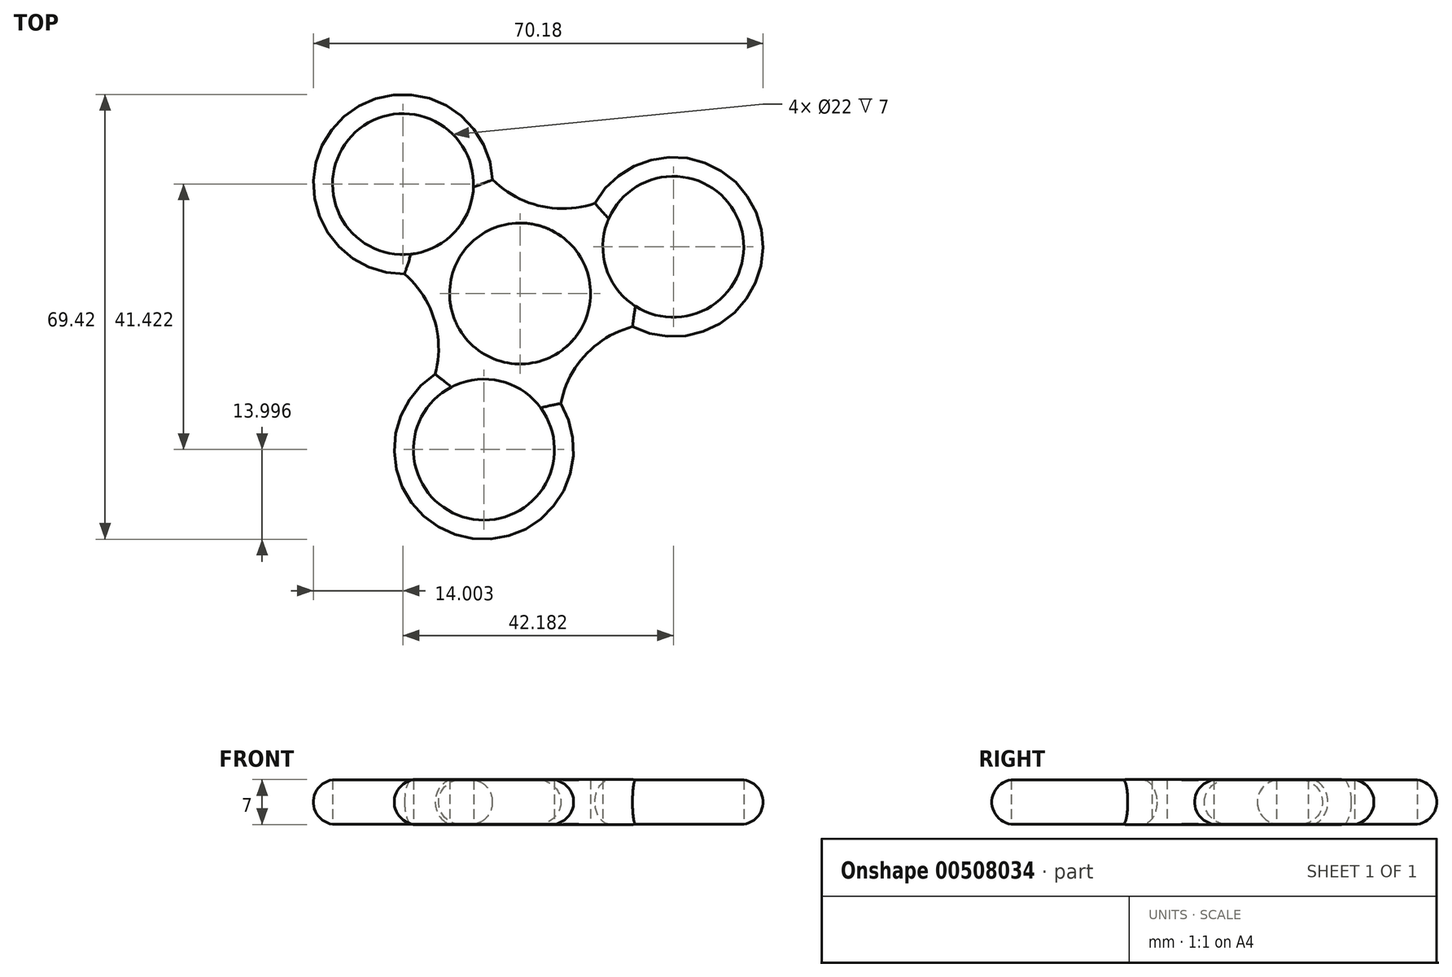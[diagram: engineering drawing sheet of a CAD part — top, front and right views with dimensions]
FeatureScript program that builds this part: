
annotation { "Feature Type Name" : "Feature", "Feature Type Description" : "" }
export const myFeature = defineFeature(function(context is Context, id is Id, definition is map)
    precondition{}
    {
        {
            var Q0;
            Q0=qCreatedBy(makeId("Top.planeOp"),FACE);
            var sketch = newSketch(context, id + "F0", { "sketchPlane" : qUnion([Q0])});
            skCircle(sketch, "E0", {"center": v(0, 0) * mm, "radius": 11 * mm});
            skLineSegment(sketch, "E1", {"start": v(0, 0) * mm, "end": v(-18.27, 17.07) * mm});
            skLineSegment(sketch, "E2", {"start": v(0, 0) * mm, "end": v(23.91, 7.29) * mm});
            skLineSegment(sketch, "E3", {"start": v(0, 0) * mm, "end": v(-5.65, -24.35) * mm});
            skCircle(sketch, "E4", {"center": v(-18.27, 17.07) * mm, "radius": 11 * mm});
            skCircle(sketch, "E5", {"center": v(23.91, 7.29) * mm, "radius": 11 * mm});
            skCircle(sketch, "E6", {"center": v(-5.65, -24.35) * mm, "radius": 11 * mm});
            skCircle(sketch, "E7", {"center": v(0, 0) * mm, "radius": 14 * mm});
            skCircle(sketch, "E8", {"center": v(-18.27, 17.07) * mm, "radius": 14 * mm});
            skCircle(sketch, "E9", {"center": v(23.91, 7.29) * mm, "radius": 14 * mm});
            skCircle(sketch, "E10", {"center": v(-5.65, -24.35) * mm, "radius": 14 * mm});
            skLineSegment(sketch, "E11", {"start": v(-18.27, 17.07) * mm, "end": v(-8.7, 27.3) * mm});
            skLineSegment(sketch, "E12", {"start": v(23.91, 7.29) * mm, "end": v(19.84, 20.68) * mm});
            skLineSegment(sketch, "E13", {"start": v(-5.65, -24.35) * mm, "end": v(7.99, -27.52) * mm});
            skLineSegment(sketch, "E14", {"start": v(-5.65, -24.35) * mm, "end": v(-19.29, -21.2) * mm});
            skLineSegment(sketch, "E15", {"start": v(-18.27, 17.07) * mm, "end": v(-27.82, 6.84) * mm});
            skLineSegment(sketch, "E16", {"start": v(23.91, 7.29) * mm, "end": v(28, -6.1) * mm});
            skArc(sketch, "E17", {"start": v(-8.7, 27.3) * mm, "mid": v(3.16, 13.64) * mm, "end": v(19.84, 20.68) * mm});
            skArc(sketch, "E18", {"start": v(-19.29, -21.2) * mm, "mid": v(-13.4, -4.08) * mm, "end": v(-27.82, 6.84) * mm});
            skArc(sketch, "E19", {"start": v(28, -6.1) * mm, "mid": v(10.23, -9.56) * mm, "end": v(7.99, -27.52) * mm});
            skSolve(sketch);
        }
        {
            var Q0;
            {var subQ0=sQuery(id+"F0.wireOp",EDGE,"E17");var subQ1=sQuery(id+"F0.wireOp",EDGE,"E7");var subQ2=makeQuery(id+"F0.imprint","INTERSECT",VERTEX,{"derivedFrom":[subQ1,subQ0]});Q0=makeQuery(id+"F0.imprint","IMPRINT",FACE,{"disambiguationData":[TD([[makeQuery(id+"F0.imprint","IMPRINT",EDGE,{"disambiguationData":[TD([[subQ2,1.0]])],"derivedFrom":subQ1}),-1.0]])]});}
            var Q1;
            {var subQ0=sQuery(id+"F0.wireOp",EDGE,"E17");var subQ1=sQuery(id+"F0.wireOp",EDGE,"E7");var subQ2=makeQuery(id+"F0.imprint","INTERSECT",VERTEX,{"derivedFrom":[subQ1,subQ0]});Q1=makeQuery(id+"F0.imprint","IMPRINT",FACE,{"disambiguationData":[TD([[makeQuery(id+"F0.imprint","IMPRINT",EDGE,{"disambiguationData":[TD([[subQ2,-1.0]])],"derivedFrom":subQ1}),-1.0]])]});}
            var Q2;
            {var subQ0=sQuery(id+"F0.wireOp",EDGE,"E18");var subQ1=sQuery(id+"F0.wireOp",EDGE,"E7");var subQ2=makeQuery(id+"F0.imprint","INTERSECT",VERTEX,{"derivedFrom":[subQ1,subQ0]});Q2=makeQuery(id+"F0.imprint","IMPRINT",FACE,{"disambiguationData":[TD([[makeQuery(id+"F0.imprint","IMPRINT",EDGE,{"disambiguationData":[TD([[subQ2,1.0]])],"derivedFrom":subQ1}),-1.0]])]});}
            var Q3;
            {var subQ0=sQuery(id+"F0.wireOp",EDGE,"E18");var subQ1=sQuery(id+"F0.wireOp",EDGE,"E7");var subQ2=makeQuery(id+"F0.imprint","INTERSECT",VERTEX,{"derivedFrom":[subQ1,subQ0]});Q3=makeQuery(id+"F0.imprint","IMPRINT",FACE,{"disambiguationData":[TD([[makeQuery(id+"F0.imprint","IMPRINT",EDGE,{"disambiguationData":[TD([[subQ2,-1.0]])],"derivedFrom":subQ1}),-1.0]])]});}
            var Q4;
            {var subQ0=sQuery(id+"F0.wireOp",EDGE,"E19");var subQ1=sQuery(id+"F0.wireOp",EDGE,"E7");var subQ2=makeQuery(id+"F0.imprint","INTERSECT",VERTEX,{"derivedFrom":[subQ1,subQ0]});Q4=makeQuery(id+"F0.imprint","IMPRINT",FACE,{"disambiguationData":[TD([[makeQuery(id+"F0.imprint","IMPRINT",EDGE,{"disambiguationData":[TD([[subQ2,1.0]])],"derivedFrom":subQ1}),-1.0]])]});}
            var Q5;
            {var subQ0=sQuery(id+"F0.wireOp",EDGE,"E19");var subQ1=sQuery(id+"F0.wireOp",EDGE,"E7");var subQ2=makeQuery(id+"F0.imprint","INTERSECT",VERTEX,{"derivedFrom":[subQ1,subQ0]});Q5=makeQuery(id+"F0.imprint","IMPRINT",FACE,{"disambiguationData":[TD([[makeQuery(id+"F0.imprint","IMPRINT",EDGE,{"disambiguationData":[TD([[subQ2,-1.0]])],"derivedFrom":subQ1}),-1.0]])]});}
            var Q6;
            {var subQ0=sQuery(id+"F0.wireOp",EDGE,"E15");var subQ1=sQuery(id+"F0.wireOp",EDGE,"E4");var subQ2=makeQuery(id+"F0.imprint","INTERSECT",VERTEX,{"derivedFrom":[subQ1,subQ0]});Q6=makeQuery(id+"F0.imprint","IMPRINT",FACE,{"disambiguationData":[TD([[makeQuery(id+"F0.imprint","IMPRINT",EDGE,{"disambiguationData":[TD([[subQ2,1.0]])],"derivedFrom":subQ1}),-1.0]])]});}
            var Q7;
            {var subQ0=sQuery(id+"F0.wireOp",EDGE,"E12");var subQ1=sQuery(id+"F0.wireOp",EDGE,"E5");var subQ2=makeQuery(id+"F0.imprint","INTERSECT",VERTEX,{"derivedFrom":[subQ1,subQ0]});Q7=makeQuery(id+"F0.imprint","IMPRINT",FACE,{"disambiguationData":[TD([[makeQuery(id+"F0.imprint","IMPRINT",EDGE,{"disambiguationData":[TD([[subQ2,1.0]])],"derivedFrom":subQ1}),-1.0]])]});}
            var Q8;
            {var subQ0=sQuery(id+"F0.wireOp",EDGE,"E14");var subQ1=sQuery(id+"F0.wireOp",EDGE,"E6");var subQ2=makeQuery(id+"F0.imprint","INTERSECT",VERTEX,{"derivedFrom":[subQ1,subQ0]});Q8=makeQuery(id+"F0.imprint","IMPRINT",FACE,{"disambiguationData":[TD([[makeQuery(id+"F0.imprint","IMPRINT",EDGE,{"disambiguationData":[TD([[subQ2,-1.0]])],"derivedFrom":subQ1}),-1.0]])]});}
            var Q9;
            {var subQ1=sQuery(id+"F0.wireOp",EDGE,"E7");var subQ5=makeQuery(id+"F0.imprint","INTERSECT",VERTEX,{"derivedFrom":[subQ1,sQuery(id+"F0.wireOp",EDGE,"E17")]});Q9=makeQuery(id+"F0.imprint","IMPRINT",FACE,{"disambiguationData":[TD([[makeQuery(id+"F0.imprint","IMPRINT",EDGE,{"disambiguationData":[TD([[subQ5,1.0]])],"derivedFrom":subQ1}),1.0]])]});}
            var Q10;
            {var subQ1=sQuery(id+"F0.wireOp",EDGE,"E7");var subQ5=makeQuery(id+"F0.imprint","INTERSECT",VERTEX,{"derivedFrom":[subQ1,sQuery(id+"F0.wireOp",EDGE,"E18")]});Q10=makeQuery(id+"F0.imprint","IMPRINT",FACE,{"disambiguationData":[TD([[makeQuery(id+"F0.imprint","IMPRINT",EDGE,{"disambiguationData":[TD([[subQ5,1.0]])],"derivedFrom":subQ1}),1.0]])]});}
            var Q11;
            {var subQ1=sQuery(id+"F0.wireOp",EDGE,"E7");var subQ5=makeQuery(id+"F0.imprint","INTERSECT",VERTEX,{"derivedFrom":[subQ1,sQuery(id+"F0.wireOp",EDGE,"E19")]});Q11=makeQuery(id+"F0.imprint","IMPRINT",FACE,{"disambiguationData":[TD([[makeQuery(id+"F0.imprint","IMPRINT",EDGE,{"disambiguationData":[TD([[subQ5,1.0]])],"derivedFrom":subQ1}),1.0]])]});}
            var Q12;
            {var subQ0=sQuery(id+"F0.wireOp",EDGE,"E18");var subQ1=sQuery(id+"F0.wireOp",EDGE,"E8");var subQ2=makeQuery(id+"F0.imprint","INTERSECT",VERTEX,{"derivedFrom":[subQ1,subQ0]});Q12=makeQuery(id+"F0.imprint","IMPRINT",FACE,{"disambiguationData":[TD([[makeQuery(id+"F0.imprint","IMPRINT",EDGE,{"disambiguationData":[TD([[subQ2,-1.0]])],"derivedFrom":subQ1}),1.0]])]});}
            var Q13;
            {var subQ0=sQuery(id+"F0.wireOp",EDGE,"E17");var subQ2=sQuery(id+"F0.wireOp",EDGE,"E8");var subQ6=makeQuery(id+"F0.imprint","INTERSECT",VERTEX,{"derivedFrom":[subQ2,subQ0]});Q13=makeQuery(id+"F0.imprint","IMPRINT",FACE,{"disambiguationData":[TD([[makeQuery(id+"F0.imprint","IMPRINT",EDGE,{"disambiguationData":[TD([[subQ6,1.0]])],"derivedFrom":subQ2}),1.0]])]});}
            var Q14;
            {var subQ0=sQuery(id+"F0.wireOp",EDGE,"E17");var subQ2=sQuery(id+"F0.wireOp",EDGE,"E9");var subQ6=makeQuery(id+"F0.imprint","INTERSECT",VERTEX,{"derivedFrom":[subQ2,subQ0]});Q14=makeQuery(id+"F0.imprint","IMPRINT",FACE,{"disambiguationData":[TD([[makeQuery(id+"F0.imprint","IMPRINT",EDGE,{"disambiguationData":[TD([[subQ6,-1.0]])],"derivedFrom":subQ2}),1.0]])]});}
            var Q15;
            {var subQ0=sQuery(id+"F0.wireOp",EDGE,"E19");var subQ2=sQuery(id+"F0.wireOp",EDGE,"E9");var subQ9=makeQuery(id+"F0.imprint","INTERSECT",VERTEX,{"derivedFrom":[subQ2,subQ0]});Q15=makeQuery(id+"F0.imprint","IMPRINT",FACE,{"disambiguationData":[TD([[makeQuery(id+"F0.imprint","IMPRINT",EDGE,{"disambiguationData":[TD([[subQ9,1.0]])],"derivedFrom":subQ2}),1.0]])]});}
            var Q16;
            {var subQ0=sQuery(id+"F0.wireOp",EDGE,"E19");var subQ1=sQuery(id+"F0.wireOp",EDGE,"E10");var subQ2=makeQuery(id+"F0.imprint","INTERSECT",VERTEX,{"derivedFrom":[subQ1,subQ0]});Q16=makeQuery(id+"F0.imprint","IMPRINT",FACE,{"disambiguationData":[TD([[makeQuery(id+"F0.imprint","IMPRINT",EDGE,{"disambiguationData":[TD([[subQ2,-1.0]])],"derivedFrom":subQ1}),1.0]])]});}
            var Q17;
            {var subQ0=sQuery(id+"F0.wireOp",EDGE,"E8");var subQ3=sQuery(id+"F0.wireOp",EDGE,"E7");var subQ5=makeQuery(id+"F0.imprint","INTERSECT",VERTEX,{"disambiguationData":[OD(1.0)],"derivedFrom":[subQ3,subQ0]});Q17=makeQuery(id+"F0.imprint","IMPRINT",FACE,{"disambiguationData":[TD([[makeQuery(id+"F0.imprint","IMPRINT",EDGE,{"disambiguationData":[TD([[subQ5,1.0]])],"derivedFrom":subQ3}),1.0]])]});}
            var Q18;
            {var subQ0=sQuery(id+"F0.wireOp",EDGE,"E8");var subQ3=sQuery(id+"F0.wireOp",EDGE,"E7");var subQ5=makeQuery(id+"F0.imprint","INTERSECT",VERTEX,{"disambiguationData":[OD(0.0)],"derivedFrom":[subQ3,subQ0]});Q18=makeQuery(id+"F0.imprint","IMPRINT",FACE,{"disambiguationData":[TD([[makeQuery(id+"F0.imprint","IMPRINT",EDGE,{"disambiguationData":[TD([[subQ5,-1.0]])],"derivedFrom":subQ3}),1.0]])]});}
            var Q19;
            {var subQ0=sQuery(id+"F0.wireOp",EDGE,"E9");var subQ3=sQuery(id+"F0.wireOp",EDGE,"E7");var subQ5=makeQuery(id+"F0.imprint","INTERSECT",VERTEX,{"disambiguationData":[OD(0.0)],"derivedFrom":[subQ3,subQ0]});Q19=makeQuery(id+"F0.imprint","IMPRINT",FACE,{"disambiguationData":[TD([[makeQuery(id+"F0.imprint","IMPRINT",EDGE,{"disambiguationData":[TD([[subQ5,1.0]])],"derivedFrom":subQ3}),1.0]])]});}
            var Q20;
            {var subQ0=sQuery(id+"F0.wireOp",EDGE,"E9");var subQ3=sQuery(id+"F0.wireOp",EDGE,"E7");var subQ5=makeQuery(id+"F0.imprint","INTERSECT",VERTEX,{"disambiguationData":[OD(1.0)],"derivedFrom":[subQ3,subQ0]});Q20=makeQuery(id+"F0.imprint","IMPRINT",FACE,{"disambiguationData":[TD([[makeQuery(id+"F0.imprint","IMPRINT",EDGE,{"disambiguationData":[TD([[subQ5,-1.0]])],"derivedFrom":subQ3}),1.0]])]});}
            var Q21;
            {var subQ0=sQuery(id+"F0.wireOp",EDGE,"E10");var subQ3=sQuery(id+"F0.wireOp",EDGE,"E7");var subQ5=makeQuery(id+"F0.imprint","INTERSECT",VERTEX,{"disambiguationData":[OD(1.0)],"derivedFrom":[subQ3,subQ0]});Q21=makeQuery(id+"F0.imprint","IMPRINT",FACE,{"disambiguationData":[TD([[makeQuery(id+"F0.imprint","IMPRINT",EDGE,{"disambiguationData":[TD([[subQ5,1.0]])],"derivedFrom":subQ3}),1.0]])]});}
            var Q22;
            {var subQ0=sQuery(id+"F0.wireOp",EDGE,"E10");var subQ3=sQuery(id+"F0.wireOp",EDGE,"E7");var subQ5=makeQuery(id+"F0.imprint","INTERSECT",VERTEX,{"disambiguationData":[OD(0.0)],"derivedFrom":[subQ3,subQ0]});Q22=makeQuery(id+"F0.imprint","IMPRINT",FACE,{"disambiguationData":[TD([[makeQuery(id+"F0.imprint","IMPRINT",EDGE,{"disambiguationData":[TD([[subQ5,-1.0]])],"derivedFrom":subQ3}),1.0]])]});}
            var Q23;
            {var subQ0=sQuery(id+"F0.wireOp",EDGE,"E17");var subQ1=sQuery(id+"F0.wireOp",EDGE,"E8");var subQ3=makeQuery(id+"F0.imprint","INTERSECT",VERTEX,{"derivedFrom":[subQ1,subQ0]});Q23=makeQuery(id+"F0.imprint","IMPRINT",FACE,{"disambiguationData":[TD([[makeQuery(id+"F0.imprint","IMPRINT",EDGE,{"disambiguationData":[TD([[subQ3,-1.0]])],"derivedFrom":subQ1}),1.0]])]});}
            var Q24;
            {var subQ0=sQuery(id+"F0.wireOp",EDGE,"E17");var subQ1=sQuery(id+"F0.wireOp",EDGE,"E9");var subQ3=makeQuery(id+"F0.imprint","INTERSECT",VERTEX,{"derivedFrom":[subQ1,subQ0]});Q24=makeQuery(id+"F0.imprint","IMPRINT",FACE,{"disambiguationData":[TD([[makeQuery(id+"F0.imprint","IMPRINT",EDGE,{"disambiguationData":[TD([[subQ3,1.0]])],"derivedFrom":subQ1}),1.0]])]});}
            var Q25;
            {var subQ0=sQuery(id+"F0.wireOp",EDGE,"E19");var subQ1=sQuery(id+"F0.wireOp",EDGE,"E9");var subQ3=makeQuery(id+"F0.imprint","INTERSECT",VERTEX,{"derivedFrom":[subQ1,subQ0]});Q25=makeQuery(id+"F0.imprint","IMPRINT",FACE,{"disambiguationData":[TD([[makeQuery(id+"F0.imprint","IMPRINT",EDGE,{"disambiguationData":[TD([[subQ3,-1.0]])],"derivedFrom":subQ1}),1.0]])]});}
            var Q26;
            {var subQ0=sQuery(id+"F0.wireOp",EDGE,"E19");var subQ1=sQuery(id+"F0.wireOp",EDGE,"E10");var subQ3=makeQuery(id+"F0.imprint","INTERSECT",VERTEX,{"derivedFrom":[subQ1,subQ0]});Q26=makeQuery(id+"F0.imprint","IMPRINT",FACE,{"disambiguationData":[TD([[makeQuery(id+"F0.imprint","IMPRINT",EDGE,{"disambiguationData":[TD([[subQ3,1.0]])],"derivedFrom":subQ1}),1.0]])]});}
            var Q27;
            {var subQ0=sQuery(id+"F0.wireOp",EDGE,"E18");var subQ1=sQuery(id+"F0.wireOp",EDGE,"E8");var subQ3=makeQuery(id+"F0.imprint","INTERSECT",VERTEX,{"derivedFrom":[subQ1,subQ0]});Q27=makeQuery(id+"F0.imprint","IMPRINT",FACE,{"disambiguationData":[TD([[makeQuery(id+"F0.imprint","IMPRINT",EDGE,{"disambiguationData":[TD([[subQ3,1.0]])],"derivedFrom":subQ1}),1.0]])]});}
            var Q28;
            {var subQ0=sQuery(id+"F0.wireOp",EDGE,"E18");var subQ1=sQuery(id+"F0.wireOp",EDGE,"E10");var subQ3=makeQuery(id+"F0.imprint","INTERSECT",VERTEX,{"derivedFrom":[subQ1,subQ0]});Q28=makeQuery(id+"F0.imprint","IMPRINT",FACE,{"disambiguationData":[TD([[makeQuery(id+"F0.imprint","IMPRINT",EDGE,{"disambiguationData":[TD([[subQ3,-1.0]])],"derivedFrom":subQ1}),1.0]])]});}
            var Q29;
            {var subQ2=sQuery(id+"F0.wireOp",EDGE,"E10");var subQ6=sQuery(id+"F0.wireOp",EDGE,"E7");var subQ7=makeQuery(id+"F0.imprint","INTERSECT",VERTEX,{"disambiguationData":[OD(0.0)],"derivedFrom":[subQ6,subQ2]});Q29=makeQuery(id+"F0.imprint","IMPRINT",FACE,{"disambiguationData":[TD([[makeQuery(id+"F0.imprint","IMPRINT",EDGE,{"disambiguationData":[TD([[subQ7,-1.0]])],"derivedFrom":subQ2}),1.0]])]});}
            extrude(context, id + "F1", {"entities" : qUnion([Q0, Q1, Q2, Q3, Q4, Q5, Q6, Q7, Q8, Q9, Q10, Q11, Q12, Q13, Q14, Q15, Q16, Q17, Q18, Q19, Q20, Q21, Q22, Q23, Q24, Q25, Q26, Q27, Q28, Q29]), "depth" : 7 * mm});
        }
        {
            var Q0;
            Q0=makeQuery(id+"F1.opExtrude","CAP_EDGE",EDGE,{"disambiguationData":[OSD([sQuery(id+"F0.wireOp",EDGE,"E8")])],"isStart":false});
            var Q1;
            Q1=makeQuery(id+"F1.opExtrude","CAP_EDGE",EDGE,{"disambiguationData":[OSD([sQuery(id+"F0.wireOp",EDGE,"E18")])],"isStart":false});
            var Q2;
            Q2=makeQuery(id+"F1.opExtrude","CAP_EDGE",EDGE,{"disambiguationData":[OSD([sQuery(id+"F0.wireOp",EDGE,"E8")])],"isStart":true});
            var Q3;
            Q3=makeQuery(id+"F1.opExtrude","CAP_EDGE",EDGE,{"disambiguationData":[OSD([sQuery(id+"F0.wireOp",EDGE,"E18")])],"isStart":true});
            var Q4;
            Q4=makeQuery(id+"F1.opExtrude","CAP_EDGE",EDGE,{"disambiguationData":[OSD([sQuery(id+"F0.wireOp",EDGE,"E10")])],"isStart":false});
            var Q5;
            Q5=makeQuery(id+"F1.opExtrude","CAP_EDGE",EDGE,{"disambiguationData":[OSD([sQuery(id+"F0.wireOp",EDGE,"E10")])],"isStart":true});
            var Q6;
            Q6=makeQuery(id+"F1.opExtrude","CAP_EDGE",EDGE,{"disambiguationData":[OSD([sQuery(id+"F0.wireOp",EDGE,"E17")])],"isStart":false});
            var Q7;
            Q7=makeQuery(id+"F1.opExtrude","CAP_EDGE",EDGE,{"disambiguationData":[OSD([sQuery(id+"F0.wireOp",EDGE,"E9")])],"isStart":false});
            var Q8;
            Q8=makeQuery(id+"F1.opExtrude","CAP_EDGE",EDGE,{"disambiguationData":[OSD([sQuery(id+"F0.wireOp",EDGE,"E19")])],"isStart":false});
            var Q9;
            Q9=makeQuery(id+"F1.opExtrude","CAP_EDGE",EDGE,{"disambiguationData":[OSD([sQuery(id+"F0.wireOp",EDGE,"E17")])],"isStart":true});
            var Q10;
            Q10=makeQuery(id+"F1.opExtrude","CAP_EDGE",EDGE,{"disambiguationData":[OSD([sQuery(id+"F0.wireOp",EDGE,"E9")])],"isStart":true});
            var Q11;
            Q11=makeQuery(id+"F1.opExtrude","CAP_EDGE",EDGE,{"disambiguationData":[OSD([sQuery(id+"F0.wireOp",EDGE,"E19")])],"isStart":true});
            fillet(context, id + "F2", {"entities" : qUnion([Q0, Q1, Q2, Q3, Q4, Q5, Q6, Q7, Q8, Q9, Q10, Q11]), "radius" : 3.5 * mm, "tangentPropagation" : true, "allowEdgeOverflow" : false});
        }
    });
